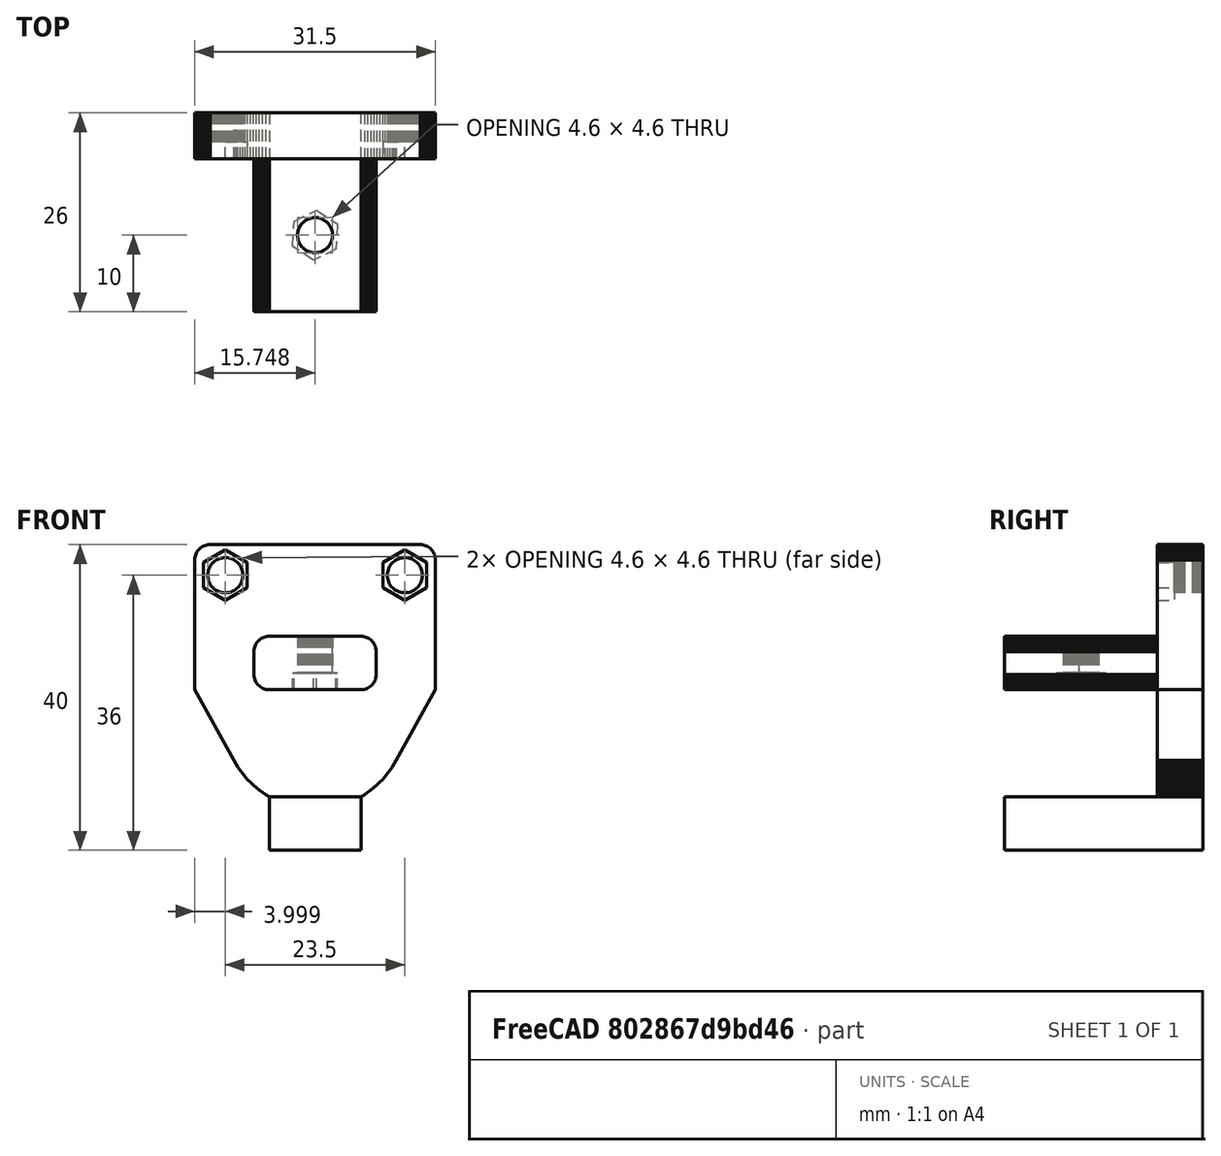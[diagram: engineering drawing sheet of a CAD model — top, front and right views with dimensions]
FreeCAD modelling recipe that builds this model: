
FCSTD DOCUMENT  (FreeCAD 1.1R44555 (Git))
Label: Ender3KasbaMount
License: All rights reserved
LicenseURL: https://en.wikipedia.org/wiki/All_rights_reserved
objects: Sketcher::SketchObject×3, Part::Feature×2, PartDesign::Pocket×2, Mesh::Feature×1, Part::Refine×1, App::Point×1, PartDesign::FeatureBase×1, PartDesign::Pad×1, PartDesign::Body×1
note: 21 computed .brp shape members not serialized (recipe doc carries the construction recipe); baked Part::Feature solids carry a one-line shape summary decoded from their .brp

FEATURE [Mesh::Feature] kusb_ender3_x_y_mount_1_  label="kusb-ender3-x-y-mount(1)"
FEATURE [Part::Feature] kusb_ender3_x_y_mount_1_001
  shape: bbox 31.5 x 26 x 40 mm, 1856 faces, 0 solids (baked)
FEATURE [Part::Refine] kusb_ender3_x_y_mount_1_002
  Source = -> kusb_ender3_x_y_mount_1_001
FEATURE [Part::Feature] kusb_ender3_x_y_mount_1_002_solid  label="kusb_ender3_x_y_mount_1_002 (Solid)"
  shape: bbox 31.5 x 26 x 40 mm, 406 faces (baked)
FEATURE [App::Point] Origin001
  Role = Origin
FEATURE [PartDesign::FeatureBase] BaseFeature
  BaseFeature = -> kusb_ender3_x_y_mount_1_002_solid
  Suppressed = false
FEATURE [Sketcher::SketchObject] Sketch
  ArcFitTolerance = 1e-06
  AttachmentSupport = -> [BaseFeature]
  ExternalTypes = [0]
  FullyConstrained = false
  MakeInternals = false
  MapMode = 5
  Placement = pos=(0,0,-12.7999) rot=(1,0,0;3.14159rad)
  sketch-geometry (4):
    g0: LineSegment StartX=7.98531 StartY=13.7592 StartZ=0 EndX=7.98531 EndY=6.28381 EndZ=0
    g1: LineSegment StartX=7.98531 StartY=6.28381 StartZ=0 EndX=15.9467 EndY=6.28381 EndZ=0
    g2: LineSegment StartX=15.9467 StartY=6.28381 StartZ=0 EndX=15.9467 EndY=13.7592 EndZ=0
    g3: LineSegment StartX=15.9467 StartY=13.7592 StartZ=0 EndX=7.98531 EndY=13.7592 EndZ=0
  constraints (8):
    c: Coincident(g0,g1)
    c: Coincident(g1,g2)
    c: Coincident(g2,g3)
    c: Coincident(g3,g0)
    c: Vertical(g0)
    c: Vertical(g2)
    c: Horizontal(g1)
    c: Horizontal(g3)
FEATURE [PartDesign::Pad] Pad
  BaseFeature = -> BaseFeature
  Direction = (0,0,-1)
  Length = 10
  Length2 = 10
  Profile = -> Sketch
  ReferenceAxis = -> Sketch [N_Axis]
  Refine = true
  SideType = 0
  Suppressed = false
  Type = 3
  Type2 = 0
  UpToFace = -> BaseFeature [Face136]
FEATURE [Sketcher::SketchObject] Sketch001
  ArcFitTolerance = 1e-06
  AttachmentSupport = -> [Pad]
  ExternalGeometry = -> [Pad]
  ExternalTypes = [0,0,0,0]
  FullyConstrained = true
  MakeInternals = false
  MapMode = 5
  Placement = pos=(0,0,-12.7999) rot=(0,0,1;0rad)
  sketch-geometry (1):
    g0: Circle CenterX=11.75 CenterY=-10 CenterZ=0 NormalX=0 NormalY=0 NormalZ=1 AngleXU=0 Radius=2.3
  constraints (3):
    c: PointOnObject(g-6,g0)
    c: PointOnObject(g-4,g0)
    c: PointOnObject(g-3,g0)
FEATURE [PartDesign::Pocket] Pocket
  BaseFeature = -> Pad
  Direction = (0,0,-1)
  Length = 5
  Length2 = 5
  Profile = -> Sketch001
  ReferenceAxis = -> Sketch001 [N_Axis]
  Refine = true
  SideType = 0
  Suppressed = false
  Type = 2
  Type2 = 0
FEATURE [Sketcher::SketchObject] Sketch002
  ArcFitTolerance = 1e-06
  AttachmentSupport = -> [Pocket]
  ExternalGeometry = -> [Pocket]
  ExternalTypes = [0]
  FullyConstrained = false
  MakeInternals = false
  MapMode = 5
  Placement = pos=(0,0,-14.9999) rot=(1,0,0;3.14159rad)
  sketch-geometry (7):
    g0: LineSegment StartX=14.6942 StartY=8.52973 StartZ=0 EndX=14.4954 EndY=11.8146 EndZ=0
    g1: LineSegment StartX=14.4954 StartY=11.8146 StartZ=0 EndX=11.5512 EndY=13.2849 EndZ=0
    g2: LineSegment StartX=11.5512 StartY=13.2849 StartZ=0 EndX=8.8058 EndY=11.4703 EndZ=0
    g3: LineSegment StartX=8.8058 StartY=11.4703 StartZ=0 EndX=9.00461 EndY=8.18539 EndZ=0
    g4: LineSegment StartX=9.00461 StartY=8.18539 StartZ=0 EndX=11.9488 EndY=6.71511 EndZ=0
    g5: LineSegment StartX=11.9488 StartY=6.71511 StartZ=0 EndX=14.6942 EndY=8.52973 EndZ=0
    g6: Circle [constr] CenterX=11.75 CenterY=10 CenterZ=0 NormalX=0 NormalY=0 NormalZ=1 AngleXU=0 Radius=3.2909
  constraints (15):
    c: Coincident(g0,g1)
    c: Coincident(g1,g2)
    c: Coincident(g2,g3)
    c: Coincident(g3,g4)
    c: Coincident(g4,g5)
    c: Coincident(g5,g0)
    c: Equal(g0, g1-g5) x5
    c: PointOnObject(g0,g6)
    c: PointOnObject(g1,g6)
    c: PointOnObject(g2,g6)
    c: PointOnObject(g3,g6)
    c: PointOnObject(g4,g6)
    c: PointOnObject(g5,g6)
    c: Coincident(g6,g-3)
    c: Distance(g1,g4) = 5.7
FEATURE [PartDesign::Pocket] Pocket001
  BaseFeature = -> Pocket
  Direction = (0,0,1)
  Length = 2.2
  Length2 = 5
  Profile = -> Sketch002
  ReferenceAxis = -> Sketch002 [N_Axis]
  Refine = true
  SideType = 0
  Suppressed = false
  Type = 0
  Type2 = 0
FEATURE [PartDesign::Body] Body
  AllowCompound = true
  BaseFeature = -> kusb_ender3_x_y_mount_1_002_solid
  Group = -> [BaseFeature,Sketch,Pad,Sketch001,Pocket,Sketch002,Pocket001]
  Origin = -> Origin
  Tip = -> Pocket001
